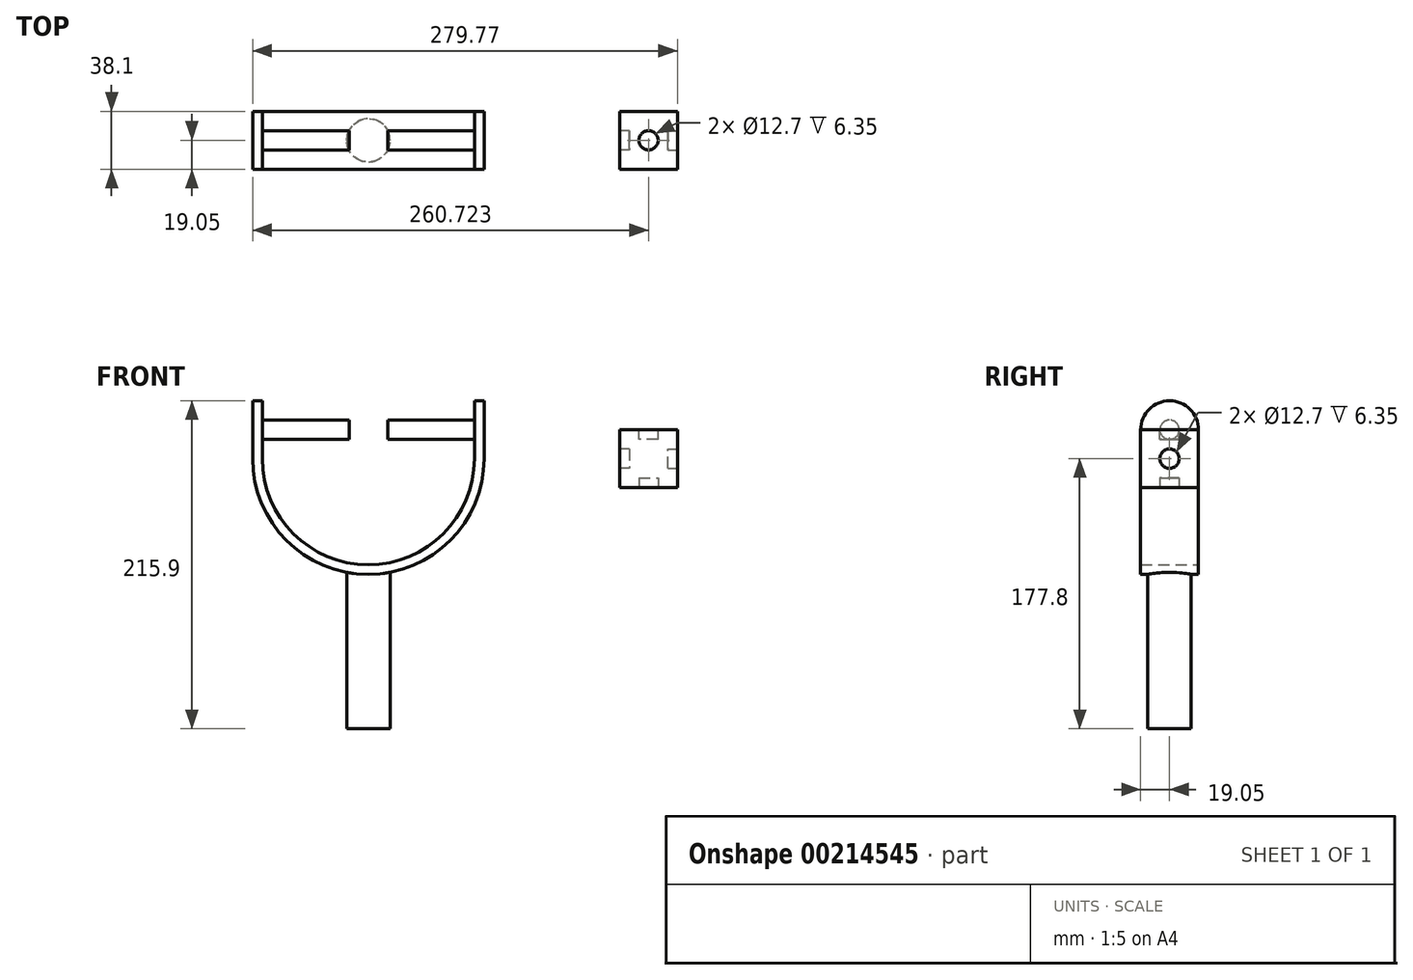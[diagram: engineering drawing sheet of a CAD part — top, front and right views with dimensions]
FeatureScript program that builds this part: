
annotation { "Feature Type Name" : "Feature", "Feature Type Description" : "" }
export const myFeature = defineFeature(function(context is Context, id is Id, definition is map)
    precondition{}
    {
        {
            var Q0;
            Q0=qCreatedBy(makeId("Front.planeOp"),FACE);
            var sketch = newSketch(context, id + "F0", { "sketchPlane" : qUnion([Q0])});
            skArc(sketch, "E0", {"start": v(-76.2, 0) * mm, "mid": v(0, -76.2) * mm, "end": v(76.2, 0) * mm});
            skArc(sketch, "E1", {"start": v(-69.85, 0) * mm, "mid": v(0, -69.85) * mm, "end": v(69.85, 0) * mm});
            skLineSegment(sketch, "E2", {"start": v(-69.85, 0) * mm, "end": v(-76.2, 0) * mm});
            skLineSegment(sketch, "E3", {"start": v(69.85, 0) * mm, "end": v(76.2, 0) * mm});
            skSolve(sketch);
        }
        {
            var Q0;
            Q0 = qSketchRegion(id + "F0", true);
            extrude(context, id + "F1", {"entities" : qUnion([Q0]), "depth" : 38.1 * mm});
        }
        {
            var Q0;
            Q0=makeQuery(id+"F1.opExtrude","SWEPT_FACE",FACE,{"disambiguationData":[OSD([sQuery(id+"F0.wireOp",EDGE,"E3")])]});
            var Q1;
            Q1=makeQuery(id+"F1.opExtrude","SWEPT_FACE",FACE,{"disambiguationData":[OSD([sQuery(id+"F0.wireOp",EDGE,"E2")])]});
            extrude(context, id + "F2", {"entities" : qUnion([Q0, Q1]), "operationType" : NewBodyOperationType.ADD, "depth" : 38.1 * mm});
        }
        {
            var Q0;
            {var subQ0=sQuery(id+"F0.wireOp",EDGE,"E3");Q0=makeQuery(id+"F2.opExtrude","CAP_EDGE",EDGE,{"disambiguationData":[OSD([subQ0]),TDD([makeQuery(id+"F1.opExtrude","CAP_EDGE",EDGE,{"disambiguationData":[OSD([subQ0])],"isStart":false})])],"isStart":false});}
            var Q1;
            {var subQ0=sQuery(id+"F0.wireOp",EDGE,"E3");Q1=makeQuery(id+"F2.opExtrude","CAP_EDGE",EDGE,{"disambiguationData":[OSD([subQ0]),TDD([makeQuery(id+"F1.opExtrude","CAP_EDGE",EDGE,{"disambiguationData":[OSD([subQ0])],"isStart":true})])],"isStart":false});}
            var Q2;
            {var subQ0=sQuery(id+"F0.wireOp",EDGE,"E2");Q2=makeQuery(id+"F2.opExtrude","CAP_EDGE",EDGE,{"disambiguationData":[OSD([subQ0]),TDD([makeQuery(id+"F1.opExtrude","CAP_EDGE",EDGE,{"disambiguationData":[OSD([subQ0])],"isStart":true})])],"isStart":false});}
            var Q3;
            {var subQ0=sQuery(id+"F0.wireOp",EDGE,"E2");Q3=makeQuery(id+"F2.opExtrude","CAP_EDGE",EDGE,{"disambiguationData":[OSD([subQ0]),TDD([makeQuery(id+"F1.opExtrude","CAP_EDGE",EDGE,{"disambiguationData":[OSD([subQ0])],"isStart":false})])],"isStart":false});}
            fillet(context, id + "F3", {"entities" : qUnion([Q0, Q1, Q2, Q3]), "radius" : 19.05 * mm, "tangentPropagation" : true, "allowEdgeOverflow" : false});
        }
        {
            var Q0;
            Q0=qCreatedBy(makeId("Right.planeOp"),FACE);
            var sketch = newSketch(context, id + "F4", { "sketchPlane" : qUnion([Q0])});
            skArc(sketch, "E4.0", {"start": v(-38.1, 19.05) * mm, "mid": v(-19.05, 38.1) * mm, "end": v(0, 19.05) * mm});
            skCircle(sketch, "E5", {"center": v(-19.05, 19.05) * mm, "radius": 6.35 * mm});
            skSolve(sketch);
        }
        {
            var Q0;
            Q0 = qSketchRegion(id + "F4", true);
            extrude(context, id + "F5", {"entities" : qUnion([Q0]), "operationType" : NewBodyOperationType.ADD, "endBound" : BoundingType.SYMMETRIC, "depth" : 139.7 * mm});
        }
        {
            var Q0;
            Q0=qCreatedBy(makeId("Right.planeOp"),FACE);
            var sketch = newSketch(context, id + "F6", { "sketchPlane" : qUnion([Q0])});
            skArc(sketch, "E6.0", {"start": v(-38.1, 19.05) * mm, "mid": v(-19.05, 38.1) * mm, "end": v(0, 19.05) * mm});
            skCircle(sketch, "E7", {"center": v(-19.05, 19.05) * mm, "radius": 6.35 * mm});
            skSolve(sketch);
        }
        {
            var Q0;
            Q0 = qSketchRegion(id + "F6", true);
            extrude(context, id + "F7", {"entities" : qUnion([Q0]), "operationType" : NewBodyOperationType.REMOVE, "endBound" : BoundingType.SYMMETRIC, "depth" : 25.4 * mm});
        }
        {
            var Q0;
            Q0=qCreatedBy(makeId("Top.planeOp"),FACE);
            cPlane(context, id + "F8", {"entities" : qUnion([Q0]), "cplaneType" : CPlaneType.OFFSET, "offset" : 190.5 * mm, "oppositeDirection" : true, "width" : 152.4 * mm, "height" : 152.4 * mm});
        }
        {
            var Q0;
            Q0=qCreatedBy(id+"F8.planeOp",FACE);
            var sketch = newSketch(context, id + "F9", { "sketchPlane" : qUnion([Q0])});
            skLineSegment(sketch, "E8.0.0", {"start": v(76.2, 0) * mm, "end": v(-76.2, 0) * mm});
            skLineSegment(sketch, "E8.0.1", {"start": v(76.2, 0) * mm, "end": v(76.2, -38.1) * mm});
            skLineSegment(sketch, "E8.0.2", {"start": v(-76.2, -38.1) * mm, "end": v(76.2, -38.1) * mm});
            skLineSegment(sketch, "E8.0.3", {"start": v(-76.2, -38.1) * mm, "end": v(-76.2, 0) * mm});
            skLineSegment(sketch, "E9", {"start": v(0, 0) * mm, "end": v(0, -19.05) * mm});
            skPoint(sketch, "E9.endSnap0", {"position": v(0, -38.1) * mm});
            skCircle(sketch, "E10", {"center": v(0, -19.05) * mm, "radius": 14.29 * mm});
            skSolve(sketch);
        }
        {
            var Q0;
            Q0=makeQuery(id+"F9.imprint","IMPRINT",FACE,{"disambiguationData":[TD([[makeQuery(id+"F9.imprint","IMPRINT",EDGE,{"derivedFrom":sQuery(id+"F9.wireOp",EDGE,"E10")}),1.0]])]});
            extrude(context, id + "F10", {"entities" : qUnion([Q0]), "operationType" : NewBodyOperationType.ADD, "endBound" : BoundingType.UP_TO_NEXT, "depth" : 25.4 * mm});
        }
        {
            var Q0;
            Q0=makeQuery(id+"F10.opExtrude","CAP_FACE",FACE,{"disambiguationData":[OSD([sQuery(id+"F9.wireOp",EDGE,"E10")])],"isStart":true});
            extrude(context, id + "F11", {"entities" : qUnion([Q0]), "operationType" : NewBodyOperationType.REMOVE, "oppositeDirection" : true, "depth" : 12.7 * mm});
        }
        {
            var Q0;
            Q0=qCreatedBy(makeId("Front.planeOp"),FACE);
            var sketch = newSketch(context, id + "F12", { "sketchPlane" : qUnion([Q0])});
            skLineSegment(sketch, "E11.bottom", {"start": v(165.47, -19.05) * mm, "end": v(203.57, -19.05) * mm});
            skLineSegment(sketch, "E11.top", {"start": v(165.47, 19.05) * mm, "end": v(203.57, 19.05) * mm});
            skLineSegment(sketch, "E11.left", {"start": v(165.47, -19.05) * mm, "end": v(165.47, 19.05) * mm});
            skLineSegment(sketch, "E11.right", {"start": v(203.57, -19.05) * mm, "end": v(203.57, 19.05) * mm});
            skPoint(sketch, "E11.middle", {"position": v(184.52, 0) * mm});
            skSolve(sketch);
        }
        {
            var Q0;
            Q0 = qSketchRegion(id + "F12", true);
            extrude(context, id + "F13", {"entities" : qUnion([Q0]), "depth" : 38.1 * mm});
        }
        {
            var Q0;
            Q0=makeQuery(id+"F13.opExtrude","SWEPT_FACE",FACE,{"disambiguationData":[OSD([sQuery(id+"F12.wireOp",EDGE,"E11.right")])]});
            var sketch = newSketch(context, id + "F14", { "sketchPlane" : qUnion([Q0])});
            skCircle(sketch, "E12", {"center": v(-19.05, 0) * mm, "radius": 6.35 * mm});
            skPoint(sketch, "E12.centerSnap0", {"position": v(-19.05, 19.05) * mm});
            skSolve(sketch);
        }
        {
            var Q0;
            Q0 = qSketchRegion(id + "F14", true);
            extrude(context, id + "F15", {"entities" : qUnion([Q0]), "operationType" : NewBodyOperationType.REMOVE, "oppositeDirection" : true, "depth" : 6.35 * mm});
        }
        {
            var Q0;
            Q0=makeQuery(id+"F13.opExtrude","SWEPT_FACE",FACE,{"disambiguationData":[OSD([sQuery(id+"F12.wireOp",EDGE,"E11.left")])]});
            var sketch = newSketch(context, id + "F16", { "sketchPlane" : qUnion([Q0])});
            skCircle(sketch, "E13", {"center": v(19.05, 0) * mm, "radius": 6.35 * mm});
            skPoint(sketch, "E13.centerSnap0", {"position": v(19.05, 19.05) * mm});
            skSolve(sketch);
        }
        {
            var Q0;
            Q0 = qSketchRegion(id + "F16", true);
            extrude(context, id + "F17", {"entities" : qUnion([Q0]), "operationType" : NewBodyOperationType.REMOVE, "oppositeDirection" : true, "depth" : 6.35 * mm});
        }
        {
            var Q0;
            Q0=makeQuery(id+"F13.opExtrude","SWEPT_FACE",FACE,{"disambiguationData":[OSD([sQuery(id+"F12.wireOp",EDGE,"E11.top")])]});
            var sketch = newSketch(context, id + "F18", { "sketchPlane" : qUnion([Q0])});
            skCircle(sketch, "E14", {"center": v(184.52, -19.05) * mm, "radius": 6.35 * mm});
            skPoint(sketch, "E14.centerSnap0", {"position": v(165.47, -19.05) * mm});
            skPoint(sketch, "E14.centerSnap1", {"position": v(184.52, -38.1) * mm});
            skSolve(sketch);
        }
        {
            var Q0;
            Q0 = qSketchRegion(id + "F18", true);
            extrude(context, id + "F19", {"entities" : qUnion([Q0]), "operationType" : NewBodyOperationType.REMOVE, "oppositeDirection" : true, "depth" : 6.35 * mm});
        }
        {
            var Q0;
            Q0=makeQuery(id+"F13.opExtrude","SWEPT_FACE",FACE,{"disambiguationData":[OSD([sQuery(id+"F12.wireOp",EDGE,"E11.bottom")])]});
            var sketch = newSketch(context, id + "F20", { "sketchPlane" : qUnion([Q0])});
            skCircle(sketch, "E15", {"center": v(184.52, 19.05) * mm, "radius": 6.35 * mm});
            skPoint(sketch, "E15.centerSnap0", {"position": v(184.52, 0) * mm});
            skPoint(sketch, "E15.centerSnap1", {"position": v(165.47, 19.05) * mm});
            skSolve(sketch);
        }
        {
            var Q0;
            Q0 = qSketchRegion(id + "F20", true);
            extrude(context, id + "F21", {"entities" : qUnion([Q0]), "operationType" : NewBodyOperationType.REMOVE, "oppositeDirection" : true, "depth" : 6.35 * mm});
        }
    });
